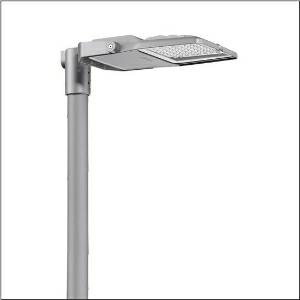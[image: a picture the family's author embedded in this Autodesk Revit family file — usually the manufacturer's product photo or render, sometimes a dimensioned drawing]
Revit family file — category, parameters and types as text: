
# Revit family: floodlight_fl_21_iq_mini___pl64_5xa7772d2e3a_5308
name_source: partatom
category: Lighting Fixtures
units: mm (PartAtom-declared; Revit-internal decimal feet)

## family parameters
Cut with Voids When Loaded = No
Host = Face
Light Source = No
Part Type = Normal
Room Calculation Point = No
Round Connector Dimension = Use Diameter
Shared = No

## types (1)
- --- (1 x LED, 17220 lm, 143 W, 3000K)
    Apparent Load = 143 VA
    CIE Flux Codes = 28 80 98 100 100
    Color Rendering = 70
    Color Temperature = 3000K
    Default Elevation = 1800 mm
    Description = Floodlight FL 21 iQ mini, floodlight, primary light control with lens, of PMMA, primary optical cover: protective disc, of toughened safety glass, transparent, light distribution: PL64, light emission: direct distribution, installation type: surface-mounted, LED, High Power LED, rated luminous flux: 17.220lm, luminous efficacy: 120lm/W, light colour: 730, colour temperature: 3000K, control gear: iQ Street-Remote/DALI, control: Auto-Match, Temp-Guard, Night-Set, Smart-Wire, Desk-Remote (wireless, voltage-free reading and setting of iQ features in the workshop via application-optimized NFC function/RFID function), optimised constant luminous flux control (CLO 2.0), Light-Fading, Lumen-Switch, with terminal, 6-pole, mains connection: 220..240V, AC, 50/60Hz, start of lifetime: 143W, end of service life: 152W, reduction: 61W, luminaire housing, of diecast aluminium, powder-coated, Siteco® metallic grey (DB 702S), corrosivity category C5 mid according to DIN EN ISO 12944, suitable for swimming pools, chlorine-resistant, sealing non-destructively replaceable, please order mast flange separately, mast bracket, of steel, galvanised, powder-coated, protection rating (complete): IP66, insulation class (complete): insulation class II (safety insulation), certification: CE, ENEC, VDE, protection symbol: D, impact resistance: IK08, permissible operating ambient temperature: -40..+40°C, permissible operating ambient temperature for outdoor applications: -40..+50°C, standard: DIN EN 12944, LABS conformity tested according to VDMA 24364:2018-05, packaging unit: 1 piece

Light Distribution: PL64
    Height = 70 mm
    Lamp = 1 x LED
    Lamp Light Flux = 17220 lm
    Lamp Power = 143 W
    Lamp count = 1
    Length = 485 mm
    Luminous efficacy = 120 lm/W
    Manufacturer = Siteco
    ModVariant = No
    Model = 5XA7772D2E3A
    Number of Poles = 1
    OnlyDefault = Yes
    Power Factor = 1
    Product Name = Floodlight FL 21 iQ mini | PL64
    Product group = floodlight | pylon annexe
    ProductGroupID = 6201
    Protection Class = Protection class II
    Protection Degree = IP 66
    RLX_Detail_Level = 1
    RLX_Emergency_Light_Flux = 0 lm
    RLX_Emergency_Type = 0
    RLX_Emergency_Type_DB = No
    RlxData = <blob elided: 101709 chars, md5=99eb6ec0>
    Socket = socket
    Standby Power = 0 W
    System Light Flux = 17220 lm
    System Power = 143 W
    Type Comments = factory setting: luminous flux: 100 % | dim-lin: 254 | 730 mA
    Type Image = l_1007125.jpg
    URL = http://relux.com
    VarID = @adj_187267
    Voltage = 0 V
    Weight = 0.00 kg
    Width = 337 mm

## geometry (parser evidence)
native form markers: Blend x4, Sweep x13
no freeform markers — native parametric forms only
